# Revit family: Keilhauer-Epix-Side_Chair_4_Leg-1
name_source: partatom
category: Furniture
revit_build: Autodesk Revit 2016 (Build: 20151007_0715(x64)
units: mm (PartAtom-declared; Revit-internal decimal feet)

## family parameters
Always vertical = Yes
Cut with Voids When Loaded = No
OmniClass Number = 23.40.70.14.64.11
OmniClass Title = Office Furniture
Room Calculation Point = No
Shared = No
Work Plane-Based = No

## types (6) — shared parameters
Assembly Code = E2020200
Depth = 21 27/32"
Height = 32 11/32"
Low Emitting Finish = Yes
Low Emitting Material = Yes
Manufacturer = Keilhauer
Product Documentation Link = https://keilhauer.com
Salvage or Reuse = Yes
Seat Pad = Yes
Type Comments = Epix
URL = https://keilhauer.com
zero-valued in all types: Percentage of Recycled Content

## per-type parameters (varying)
| type | 4-Leg Steel | 4-Leg Wood | Arms | Base | Description | Width |
| 76260 | Yes | No | No | Yes | Side chair, formed felt shell with seat pad, 4-leg steel base | 19 25/32" |
| 76261 | No | Yes | No | No | Side chair, formed felt shell with seatpad, 4-leg ash base | 18" |
| 76262 | No | Yes | No | No | Side chair, formed felt shell with seatpad, 4-leg walnut base | 18" |
| 76270 | Yes | No | Yes | Yes | Side chair, formed felt shell with arms and seatpad, 4-leg steel base | 23 3/64" |
| 76271 | No | Yes | Yes | No | Side chair, formed felt shell with arms and seatpad, 4-leg ash base | 23 3/64" |
| 76272 | No | Yes | Yes | No | Side chair, formed felt shell with arms and seatpad, 4-leg walnut base | 23 3/64" |

note: column(s) folded — value = type name in every type: Model

## geometry (parser evidence)
native form markers: Sweep x9
no freeform markers — native parametric forms only
